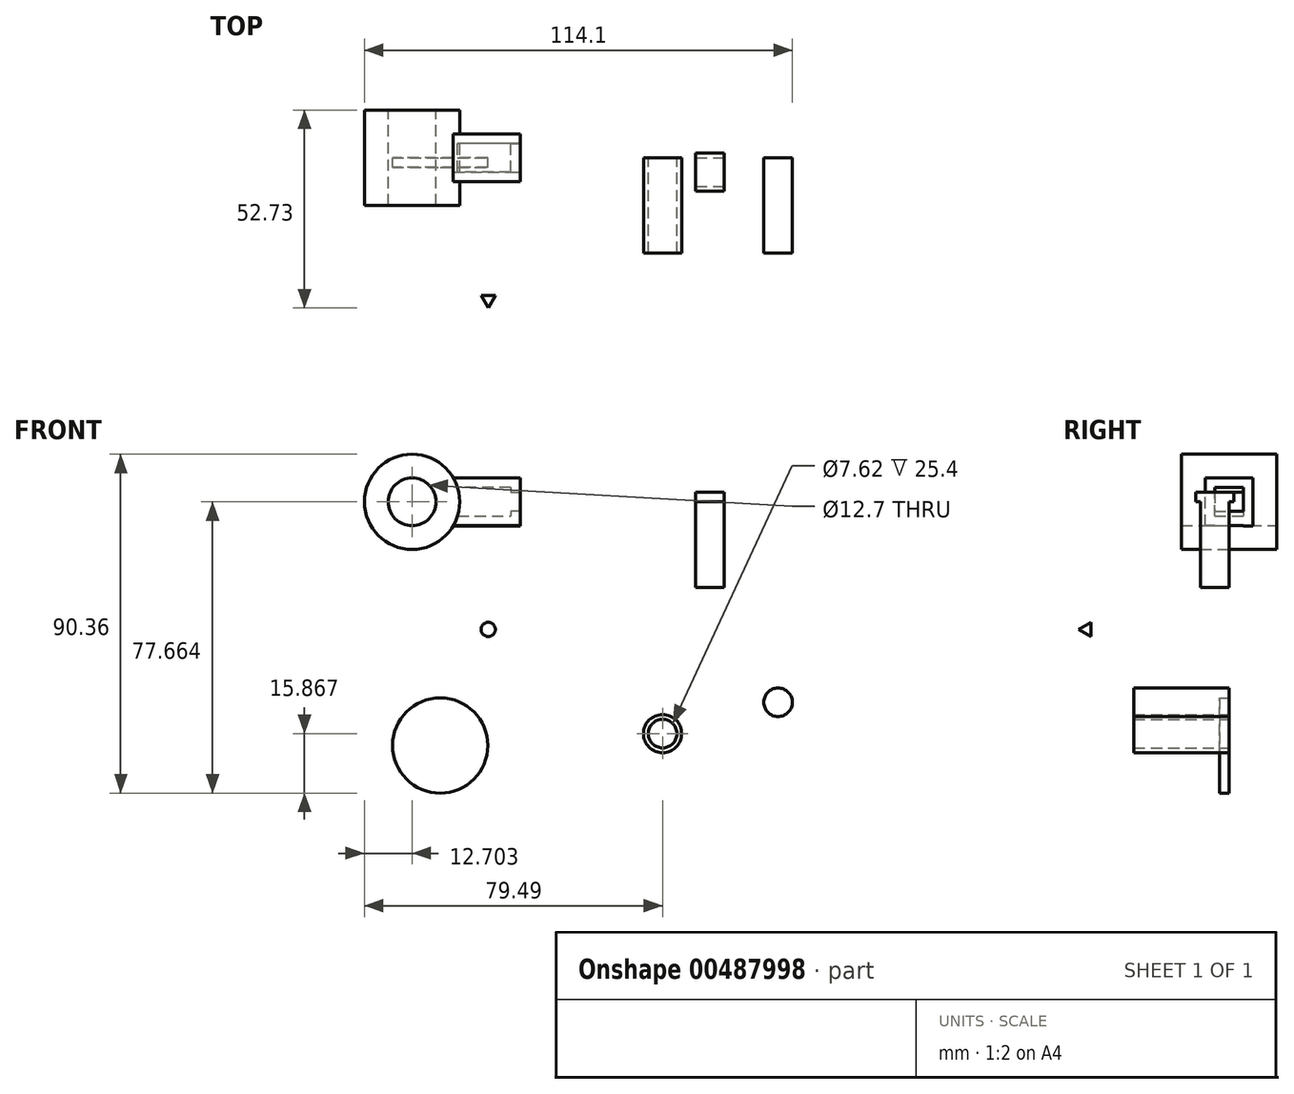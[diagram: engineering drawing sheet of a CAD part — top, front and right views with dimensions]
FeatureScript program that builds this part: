
annotation { "Feature Type Name" : "Feature", "Feature Type Description" : "" }
export const myFeature = defineFeature(function(context is Context, id is Id, definition is map)
    precondition{}
    {
        {
            var Q0;
            Q0=qCreatedBy(makeId("Front.planeOp"),FACE);
            var sketch = newSketch(context, id + "F0", { "sketchPlane" : qUnion([Q0])});
            skCircle(sketch, "E0", {"center": v(-55.7, 34.02) * mm, "radius": 6.35 * mm});
            skCircle(sketch, "E1", {"center": v(-55.7, 34.02) * mm, "radius": 12.7 * mm});
            skLineSegment(sketch, "E2", {"start": v(-55.7, 40.37) * mm, "end": v(-26.86, 40.37) * mm});
            skLineSegment(sketch, "E3", {"start": v(-55.7, 27.67) * mm, "end": v(-26.86, 27.67) * mm});
            skLineSegment(sketch, "E4", {"start": v(-26.86, 27.67) * mm, "end": v(-26.86, 30.21) * mm});
            skLineSegment(sketch, "E5", {"start": v(-26.86, 40.37) * mm, "end": v(-26.86, 37.83) * mm});
            skLineSegment(sketch, "E6", {"start": v(-26.86, 37.83) * mm, "end": v(-29.4, 37.83) * mm});
            skLineSegment(sketch, "E7", {"start": v(-26.86, 30.21) * mm, "end": v(-29.4, 30.21) * mm});
            skLineSegment(sketch, "E8", {"start": v(-29.4, 30.21) * mm, "end": v(-43.6, 30.21) * mm});
            skLineSegment(sketch, "E9", {"start": v(-29.4, 37.83) * mm, "end": v(-43.6, 37.83) * mm});
            skLineSegment(sketch, "E10", {"start": v(-29.4, 30.21) * mm, "end": v(-29.4, 31.48) * mm});
            skLineSegment(sketch, "E11", {"start": v(-29.4, 37.83) * mm, "end": v(-29.4, 36.56) * mm});
            skLineSegment(sketch, "E12", {"start": v(-26.9, 36.56) * mm, "end": v(-26.86, 37.83) * mm});
            skLineSegment(sketch, "E13", {"start": v(-26.86, 30.21) * mm, "end": v(-26.86, 31.48) * mm});
            skLineSegment(sketch, "E14", {"start": v(-29.4, 31.48) * mm, "end": v(-26.86, 31.48) * mm});
            skLineSegment(sketch, "E15", {"start": v(-29.4, 36.56) * mm, "end": v(-26.9, 36.56) * mm});
            skSolve(sketch);
        }
        {
            var Q0;
            {var subQ0=sQuery(id+"F0.wireOp",EDGE,"E2");var subQ1=sQuery(id+"F0.wireOp",EDGE,"E0");var subQ2=makeQuery(id+"F0.imprint","INTERSECT",VERTEX,{"derivedFrom":[subQ1,subQ0]});Q0=makeQuery(id+"F0.imprint","IMPRINT",FACE,{"disambiguationData":[TD([[makeQuery(id+"F0.imprint","IMPRINT",EDGE,{"disambiguationData":[TD([[subQ2,-1.0]])],"derivedFrom":subQ1}),-1.0]])]});}
            var Q1;
            {var subQ5=sQuery(id+"F0.wireOp",EDGE,"E2");var subQ7=sQuery(id+"F0.wireOp",EDGE,"E0");var subQ8=makeQuery(id+"F0.imprint","INTERSECT",VERTEX,{"derivedFrom":[subQ7,subQ5]});Q1=makeQuery(id+"F0.imprint","IMPRINT",FACE,{"disambiguationData":[TD([[makeQuery(id+"F0.imprint","IMPRINT",EDGE,{"disambiguationData":[TD([[subQ8,1.0]])],"derivedFrom":subQ7}),-1.0]])]});}
            extrude(context, id + "F1", {"entities" : qUnion([Q0, Q1]), "endBound" : BoundingType.SYMMETRIC, "depth" : 25.4 * mm, "offsetDistance" : 25.4 * mm});
        }
        {
            var Q0;
            Q0 = qSketchRegion(id + "F0", true);
            extrude(context, id + "F2", {"entities" : qUnion([Q0]), "operationType" : NewBodyOperationType.ADD, "endBound" : BoundingType.SYMMETRIC, "depth" : 12.7 * mm, "offsetDistance" : 25.4 * mm});
        }
        {
            var Q0;
            {var subQ0=sQuery(id+"F0.wireOp",EDGE,"E5");var subQ1=sQuery(id+"F0.wireOp",EDGE,"E9");var subQ2=sQuery(id+"F0.wireOp",EDGE,"E1");var subQ3=sQuery(id+"F0.wireOp",EDGE,"E2");var subQ4=sQuery(id+"F0.wireOp",EDGE,"E11");var subQ5=sQuery(id+"F0.wireOp",EDGE,"E12");var subQ6=sQuery(id+"F0.wireOp",EDGE,"E15");Q0=makeQuery(id+"F2.boolean.opBoolean","SPLIT",FACE,{"disambiguationData":[TD([makeQuery(id+"F2.opExtrude","SWEPT_FACE",FACE,{"disambiguationData":[OSD([subQ3])]})])],"derivedFrom":makeQuery(id+"F2.opExtrude","CAP_FACE",FACE,{"disambiguationData":[OSD([sQuery(id+"F0.wireOp",EDGE,"E0"),subQ2,subQ3,sQuery(id+"F0.wireOp",EDGE,"E3"),sQuery(id+"F0.wireOp",EDGE,"E4"),subQ0,sQuery(id+"F0.wireOp",EDGE,"E8"),subQ1,sQuery(id+"F0.wireOp",EDGE,"E10"),subQ4,subQ5,sQuery(id+"F0.wireOp",EDGE,"E13"),sQuery(id+"F0.wireOp",EDGE,"E14"),subQ6])],"isStart":false})});}
            var sketch = newSketch(context, id + "F3", { "sketchPlane" : qUnion([Q0])});
            skLineSegment(sketch, "E16.bottom", {"start": v(-26.86, 40.37) * mm, "end": v(-44.7, 40.37) * mm});
            skLineSegment(sketch, "E16.top", {"start": v(-26.86, 27.65) * mm, "end": v(-44.7, 27.65) * mm});
            skLineSegment(sketch, "E16.left", {"start": v(-26.86, 40.37) * mm, "end": v(-26.86, 27.65) * mm});
            skLineSegment(sketch, "E16.right", {"start": v(-44.7, 40.37) * mm, "end": v(-44.7, 27.65) * mm});
            skSolve(sketch);
        }
        {
            var Q0;
            Q0 = qSketchRegion(id + "F3", true);
            extrude(context, id + "F4", {"entities" : qUnion([Q0]), "operationType" : NewBodyOperationType.ADD, "oppositeDirection" : true, "depth" : 2.54 * mm, "offsetDistance" : 25.4 * mm});
        }
        {
            var Q0;
            {var subQ0=sQuery(id+"F0.wireOp",EDGE,"E5");var subQ1=sQuery(id+"F0.wireOp",EDGE,"E9");var subQ2=sQuery(id+"F0.wireOp",EDGE,"E1");var subQ3=sQuery(id+"F0.wireOp",EDGE,"E2");var subQ4=sQuery(id+"F0.wireOp",EDGE,"E11");var subQ5=sQuery(id+"F0.wireOp",EDGE,"E12");var subQ6=sQuery(id+"F0.wireOp",EDGE,"E15");Q0=makeQuery(id+"F2.boolean.opBoolean","SPLIT",FACE,{"disambiguationData":[TD([makeQuery(id+"F2.opExtrude","SWEPT_FACE",FACE,{"disambiguationData":[OSD([subQ3])]})])],"derivedFrom":makeQuery(id+"F2.opExtrude","CAP_FACE",FACE,{"disambiguationData":[OSD([sQuery(id+"F0.wireOp",EDGE,"E0"),subQ2,subQ3,sQuery(id+"F0.wireOp",EDGE,"E3"),sQuery(id+"F0.wireOp",EDGE,"E4"),subQ0,sQuery(id+"F0.wireOp",EDGE,"E8"),subQ1,sQuery(id+"F0.wireOp",EDGE,"E10"),subQ4,subQ5,sQuery(id+"F0.wireOp",EDGE,"E13"),sQuery(id+"F0.wireOp",EDGE,"E14"),subQ6])],"isStart":true})});}
            var sketch = newSketch(context, id + "F5", { "sketchPlane" : qUnion([Q0])});
            skLineSegment(sketch, "E17.bottom", {"start": v(26.86, 40.37) * mm, "end": v(44.7, 40.37) * mm});
            skLineSegment(sketch, "E17.top", {"start": v(26.86, 27.52) * mm, "end": v(44.7, 27.52) * mm});
            skLineSegment(sketch, "E17.left", {"start": v(26.86, 40.37) * mm, "end": v(26.86, 27.52) * mm});
            skLineSegment(sketch, "E17.right", {"start": v(44.7, 40.37) * mm, "end": v(44.7, 27.52) * mm});
            skSolve(sketch);
        }
        {
            var Q0;
            {var subQ4=sQuery(id+"F5.wireOp",EDGE,"E17.top");Q0=makeQuery(id+"F5.imprint","IMPRINT",FACE,{"disambiguationData":[TD([[makeQuery(id+"F5.imprint","IMPRINT",EDGE,{"derivedFrom":subQ4}),1.0]])]});}
            extrude(context, id + "F6", {"entities" : qUnion([Q0]), "operationType" : NewBodyOperationType.ADD, "oppositeDirection" : true, "depth" : 2.54 * mm, "offsetDistance" : 25.4 * mm});
        }
        {
            var Q0;
            Q0=qCreatedBy(makeId("Front.planeOp"),FACE);
            var sketch = newSketch(context, id + "F7", { "sketchPlane" : qUnion([Q0])});
            skLineSegment(sketch, "E18", {"start": v(19.94, 36.6) * mm, "end": v(19.94, 11.2) * mm});
            skLineSegment(sketch, "E19", {"start": v(19.94, 11.2) * mm, "end": v(27.56, 11.2) * mm});
            skLineSegment(sketch, "E20", {"start": v(27.56, 11.2) * mm, "end": v(27.56, 36.6) * mm});
            skLineSegment(sketch, "E21", {"start": v(19.94, 36.6) * mm, "end": v(27.56, 36.6) * mm});
            skSolve(sketch);
        }
        {
            var Q0;
            Q0=makeQuery(id+"F7.imprint","IMPRINT",FACE,{"disambiguationData":[TD([[makeQuery(id+"F7.imprint","IMPRINT",EDGE,{"derivedFrom":sQuery(id+"F7.wireOp",EDGE,"E18")}),1.0]])]});
            extrude(context, id + "F8", {"entities" : qUnion([Q0]), "depth" : 7.62 * mm, "offsetDistance" : 25.4 * mm});
        }
        {
            var Q0;
            Q0=makeQuery(id+"F8.opExtrude","SWEPT_FACE",FACE,{"disambiguationData":[OSD([sQuery(id+"F7.wireOp",EDGE,"E21")])]});
            var sketch = newSketch(context, id + "F9", { "sketchPlane" : qUnion([Q0])});
            skLineSegment(sketch, "E22", {"start": v(19.94, 0) * mm, "end": v(19.94, 1.27) * mm});
            skLineSegment(sketch, "E23", {"start": v(27.56, 1.27) * mm, "end": v(27.56, 0) * mm});
            skLineSegment(sketch, "E24", {"start": v(27.56, -7.62) * mm, "end": v(27.56, -8.89) * mm});
            skLineSegment(sketch, "E25", {"start": v(19.94, -8.9) * mm, "end": v(19.94, -7.62) * mm});
            skLineSegment(sketch, "E26", {"start": v(19.94, 1.27) * mm, "end": v(27.56, 1.27) * mm});
            skLineSegment(sketch, "E27", {"start": v(19.94, -8.9) * mm, "end": v(27.56, -8.89) * mm});
            skSolve(sketch);
        }
        {
            var Q0;
            Q0 = qSketchRegion(id + "F9", true);
            var Q1;
            Q1=makeQuery(id+"F9.imprint","IMPRINT",FACE,{"disambiguationData":[TD([[makeQuery(id+"F9.imprint","IMPRINT",EDGE,{"derivedFrom":sQuery(id+"F9.wireOp",EDGE,"E22")}),-1.0]])]});
            var Q2;
            Q2=makeQuery(id+"F9.imprint","IMPRINT",FACE,{"disambiguationData":[TD([[makeQuery(id+"F9.imprint","IMPRINT",EDGE,{"derivedFrom":sQuery(id+"F9.wireOp",EDGE,"E24")}),-1.0]])]});
            extrude(context, id + "F10", {"entities" : qUnion([Q0, Q1, Q2]), "operationType" : NewBodyOperationType.ADD, "oppositeDirection" : true, "depth" : 2.54 * mm, "offsetDistance" : 25.4 * mm});
        }
        {
            var Q0;
            Q0=qCreatedBy(makeId("Front.planeOp"),FACE);
            var sketch = newSketch(context, id + "F11", { "sketchPlane" : qUnion([Q0])});
            skCircle(sketch, "E28", {"center": v(-48.2, -30.94) * mm, "radius": 12.7 * mm});
            skSolve(sketch);
        }
        {
            var Q0;
            Q0 = qSketchRegion(id + "F11", true);
            extrude(context, id + "F12", {"entities" : qUnion([Q0]), "depth" : 2.54 * mm, "offsetDistance" : 25.4 * mm});
        }
        {
            var Q0;
            Q0=qCreatedBy(makeId("Front.planeOp"),FACE);
            var sketch = newSketch(context, id + "F13", { "sketchPlane" : qUnion([Q0])});
            skCircle(sketch, "E29", {"center": v(11.08, -27.77) * mm, "radius": 5.08 * mm});
            skCircle(sketch, "E30", {"center": v(11.08, -27.77) * mm, "radius": 3.81 * mm});
            skSolve(sketch);
        }
        {
            var Q0;
            Q0 = qSketchRegion(id + "F13", true);
            extrude(context, id + "F14", {"entities" : qUnion([Q0]), "depth" : 25.4 * mm, "offsetDistance" : 25.4 * mm});
        }
        {
            var Q0;
            Q0=qCreatedBy(makeId("Front.planeOp"),FACE);
            var sketch = newSketch(context, id + "F15", { "sketchPlane" : qUnion([Q0])});
            skCircle(sketch, "E31", {"center": v(41.88, -19.43) * mm, "radius": 3.81 * mm});
            skSolve(sketch);
        }
        {
            var Q0;
            Q0=makeQuery(id+"F15.imprint","IMPRINT",FACE,{"disambiguationData":[TD([[makeQuery(id+"F15.imprint","IMPRINT",EDGE,{"derivedFrom":sQuery(id+"F15.wireOp",EDGE,"E31")}),1.0]])]});
            extrude(context, id + "F16", {"entities" : qUnion([Q0]), "depth" : 25.4 * mm, "offsetDistance" : 25.4 * mm});
        }
        {
            var Q0;
            Q0=qCreatedBy(makeId("Top.planeOp"),FACE);
            var sketch = newSketch(context, id + "F17", { "sketchPlane" : qUnion([Q0])});
            skLineSegment(sketch, "E32", {"start": v(-37.3, -36.73) * mm, "end": v(-33.5, -36.73) * mm});
            skLineSegment(sketch, "E33", {"start": v(-35.4, -36.73) * mm, "end": v(-35.4, -40.03) * mm});
            skLineSegment(sketch, "E34", {"start": v(-35.4, -40.03) * mm, "end": v(-37.3, -36.73) * mm});
            skSolve(sketch);
        }
        {
            var Q0;
            Q0 = qSketchRegion(id + "F17", true);
            var Q1;
            Q1=sQuery(id+"F17.wireOp",EDGE,"E33");
            revolve(context, id + "F18", {"surfaceOperationType" : NewSurfaceOperationType.NEW, "entities" : qUnion([Q0]), "axis" : qUnion([Q1]), "revolveType" : RevolveType.FULL});
        }
    });
